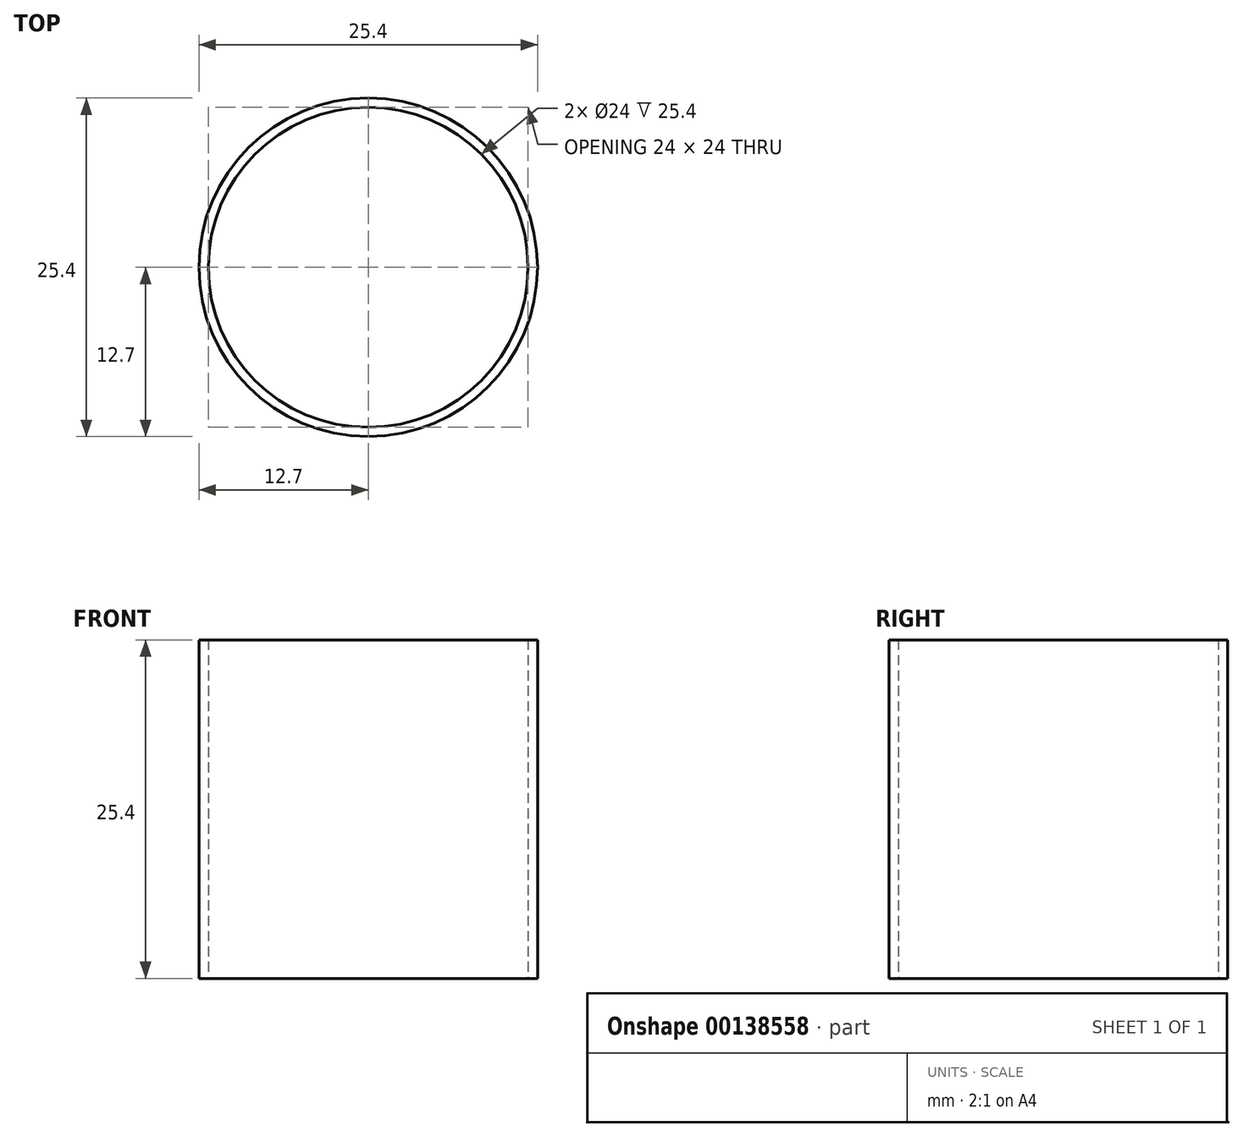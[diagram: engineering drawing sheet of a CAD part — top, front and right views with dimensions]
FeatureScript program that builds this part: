
annotation { "Feature Type Name" : "Feature", "Feature Type Description" : "" }
export const myFeature = defineFeature(function(context is Context, id is Id, definition is map)
    precondition{}
    {
        {
            var Q0;
            Q0=qCreatedBy(makeId("Top.planeOp"),FACE);
            var sketch = newSketch(context, id + "F0", { "sketchPlane" : qUnion([Q0])});
            skCircle(sketch, "E0", {"center": v(0, 0) * mm, "radius": 12.7 * mm});
            skSolve(sketch);
        }
        {
            var Q0;
            Q0=makeQuery(id+"F0.imprint","IMPRINT",FACE,{"disambiguationData":[TD([[makeQuery(id+"F0.imprint","IMPRINT",EDGE,{"derivedFrom":sQuery(id+"F0.wireOp",EDGE,"E0")}),1.0]])]});
            extrude(context, id + "F1", {"entities" : qUnion([Q0]), "depth" : 25.4 * mm});
        }
        {
            var Q0;
            Q0=sQuery(id+"F0.wireOp",VERTEX,"E0.center");
            var Q1;
            Q1=makeQuery(id+"F1.opExtrude","SWEPT_BODY",BODY,{"disambiguationData":[OSD([sQuery(id+"F0.wireOp",EDGE,"E0")])]});
            hole(context, id + "F2", {"style" : HoleStyle.SIMPLE, "endStyle" : HoleEndStyle.THROUGH, "oppositeDirection" : true, "holeDiameter" : 24 * mm, "locations" : qUnion([Q0]), "scope" : qUnion([Q1]), "isTappedThrough" : true});
        }
    });
